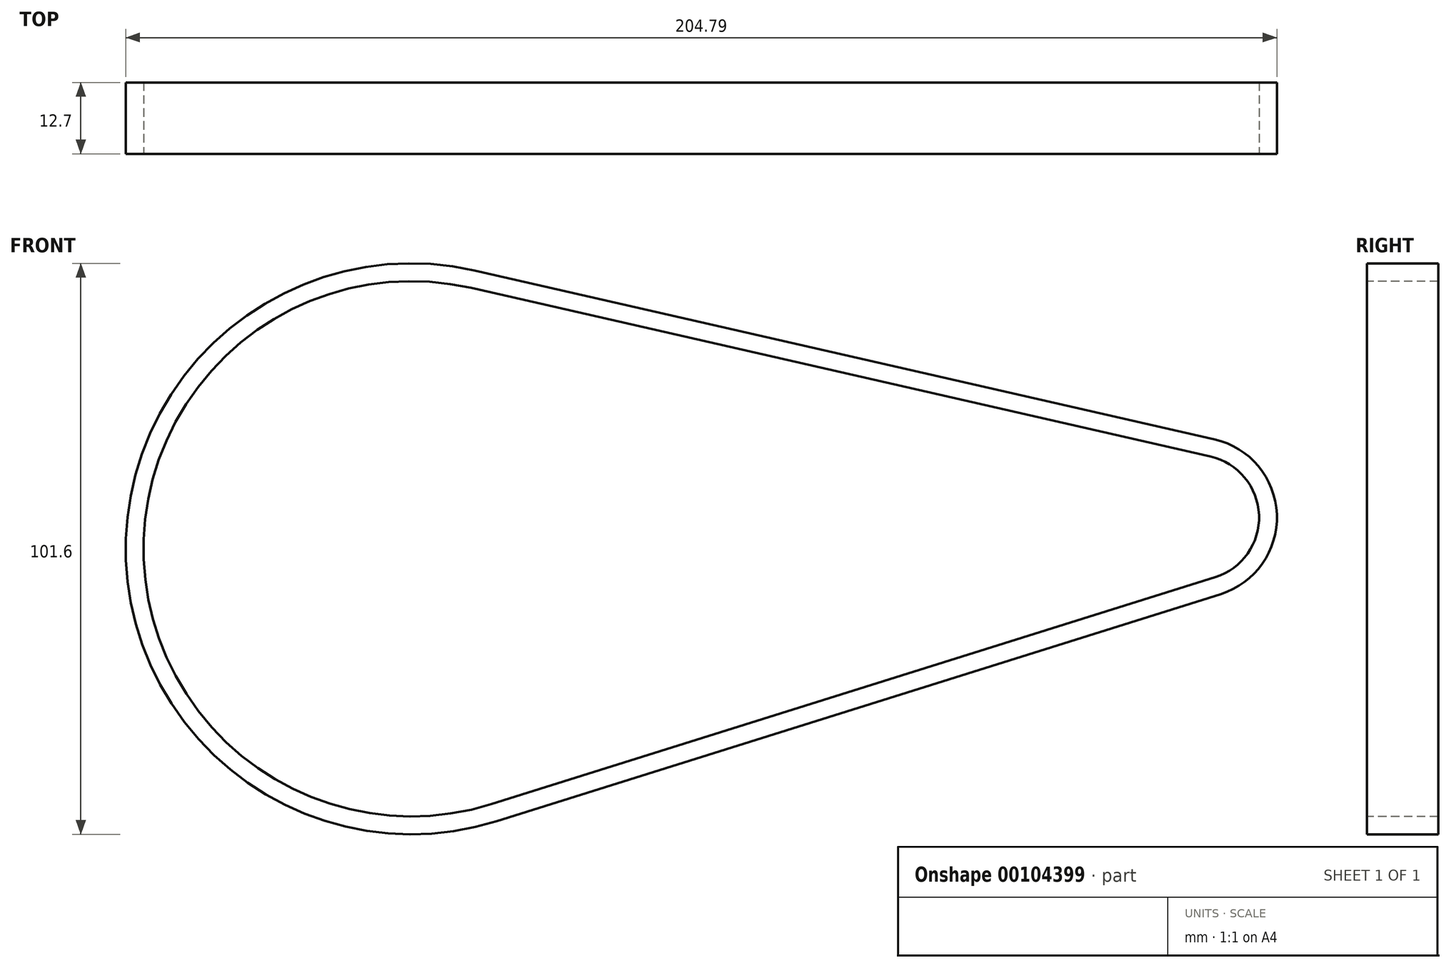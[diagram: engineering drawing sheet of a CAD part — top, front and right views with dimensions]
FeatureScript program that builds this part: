
annotation { "Feature Type Name" : "Feature", "Feature Type Description" : "" }
export const myFeature = defineFeature(function(context is Context, id is Id, definition is map)
    precondition{}
    {
        {
            var Q0;
            Q0=qCreatedBy(makeId("Front.planeOp"),FACE);
            var sketch = newSketch(context, id + "F0", { "sketchPlane" : qUnion([Q0])});
            skArc(sketch, "E0", {"start": v(11.3, 49.53) * mm, "mid": v(-50.76, -2.02) * mm, "end": v(15.2, -48.47) * mm});
            skArc(sketch, "E1", {"start": v(143.98, -8.06) * mm, "mid": v(153.98, 6.14) * mm, "end": v(142.88, 19.5) * mm});
            skLineSegment(sketch, "E2", {"start": v(78.41, -51.04) * mm, "end": v(78.04, -49.33) * mm});
            skLineSegment(sketch, "E3", {"start": v(11.3, 49.53) * mm, "end": v(142.88, 19.5) * mm});
            skLineSegment(sketch, "E4", {"start": v(15.2, -48.47) * mm, "end": v(143.98, -8.06) * mm});
            skLineSegment(sketch, "E5.0", {"start": v(10.6, 46.43) * mm, "end": v(142.17, 16.4) * mm});
            skArc(sketch, "E5.1", {"start": v(10.6, 46.43) * mm, "mid": v(-47.59, -1.9) * mm, "end": v(14.26, -45.44) * mm});
            skLineSegment(sketch, "E5.2", {"start": v(14.26, -45.44) * mm, "end": v(143.03, -5.04) * mm});
            skArc(sketch, "E5.3", {"start": v(143.03, -5.04) * mm, "mid": v(150.8, 6.01) * mm, "end": v(142.17, 16.4) * mm});
            skSolve(sketch);
        }
        {
            var Q0;
            Q0=sQuery(id+"F0.wireOp",EDGE,"E5.1");
            var Q1;
            Q1=sQuery(id+"F0.wireOp",EDGE,"E0");
            var Q2;
            Q2=sQuery(id+"F0.wireOp",EDGE,"E5.0");
            var Q3;
            Q3=sQuery(id+"F0.wireOp",EDGE,"E3");
            var Q4;
            Q4=sQuery(id+"F0.wireOp",EDGE,"E1");
            var Q5;
            Q5=sQuery(id+"F0.wireOp",EDGE,"E5.3");
            var Q6;
            Q6=sQuery(id+"F0.wireOp",EDGE,"E5.2");
            var Q7;
            Q7=sQuery(id+"F0.wireOp",EDGE,"E4");
            extrude(context, id + "F1", {"bodyType" : ToolBodyType.SURFACE, "surfaceEntities" : qUnion([Q0, Q1, Q2, Q3, Q4, Q5, Q6, Q7]), "depth" : 12.7 * mm});
        }
    });
